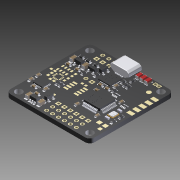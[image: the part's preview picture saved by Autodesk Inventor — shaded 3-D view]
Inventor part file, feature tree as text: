
AUTODESK INVENTOR PART (.ipt)
format: ipt  version: 2015 (Build 190159000, 159)  size: 8,326,656 bytes
history: native  units: in
note: dims shown in document units (in); Inventor stores cm internally (conversion verified against a paired STEP export)
features: imported_body x50, extrude x2, other x1, sketch x1
ambient origin geometry x8: Origin, YZ Plane, XZ Plane, XY Plane, X Axis, Y Axis, Z Axis, Center Point
bodies: Solid2 (feature_tree), Solid3 (feature_tree), Solid4 (feature_tree), Solid5 (feature_tree), Solid6 (feature_tree), Solid7 (feature_tree), Solid8 (feature_tree), Solid9 (feature_tree), Solid10 (feature_tree), Solid11 (feature_tree), Solid12 (feature_tree), Solid13 (feature_tree), Solid14 (feature_tree), Solid15 (feature_tree), Solid16 (feature_tree), Solid17 (feature_tree), Solid18 (feature_tree), Solid19 (feature_tree), Solid20 (feature_tree), Solid21 (feature_tree), Solid22 (feature_tree), Solid23 (feature_tree), Solid24 (feature_tree), Solid25 (feature_tree), Solid26 (feature_tree), Solid27 (feature_tree), Solid28 (feature_tree), Solid29 (feature_tree), Solid30 (feature_tree), Solid31 (feature_tree), Solid32 (feature_tree), Solid33 (feature_tree), Solid34 (feature_tree), Solid35 (feature_tree), Solid36 (feature_tree), Solid37 (feature_tree), Solid38 (feature_tree), Solid39 (feature_tree), Solid40 (feature_tree), Solid41 (feature_tree), Solid42 (feature_tree), Solid43 (feature_tree), Solid44 (feature_tree), Solid45 (feature_tree), Solid46 (feature_tree), Solid47 (feature_tree), Solid48 (feature_tree), Solid49 (feature_tree), Solid50 (feature_tree)
feature tree (54):
  other  "Naze32 Acro1"
  sketch  "Sketch1"  dims[d3=1.2008in d4=1.2008in d5=0.0709in d6=0.0in d7=0.1181in d8=0.1181in d9=0.1181in d10=0.1181in d11=0.0709in d12=0.0in]
  extrude  "Extrusion1"  Depth=0.0709in
  extrude  "Extrusion2"  Depth=0.0709in TaperAngle=0.0deg
  imported_body  "Base1"
  imported_body  "Base2"
  imported_body  "Base3"
  imported_body  "Base4"
  imported_body  "Base5"
  imported_body  "Base6"
  imported_body  "Base7"
  imported_body  "Base8"
  imported_body  "Base9"
  imported_body  "Base10"
  imported_body  "Base11"
  imported_body  "Base12"
  imported_body  "Base13"
  imported_body  "Base14"
  imported_body  "Base15"
  imported_body  "Base16"
  imported_body  "Base17"
  imported_body  "Base18"
  imported_body  "Base19"
  imported_body  "Base20"
  imported_body  "Base21"
  imported_body  "Base22"
  imported_body  "Base23"
  imported_body  "Base24"
  imported_body  "Base25"
  imported_body  "Base26"
  imported_body  "Base27"
  imported_body  "Base28"
  imported_body  "Base29"
  imported_body  "Base30"
  imported_body  "Base31"
  imported_body  "Base32"
  imported_body  "Base33"
  imported_body  "Base34"
  imported_body  "Base35"
  imported_body  "Base36"
  imported_body  "Base37"
  imported_body  "Base38"
  imported_body  "Base39"
  imported_body  "Base40"
  imported_body  "Base41"
  imported_body  "Base42"
  imported_body  "Base43"
  imported_body  "Base44"
  imported_body  "Base45"
  imported_body  "Base46"
  imported_body  "Base47"
  imported_body  "Base48"
  imported_body  "Base49"
  imported_body  "Base50"
